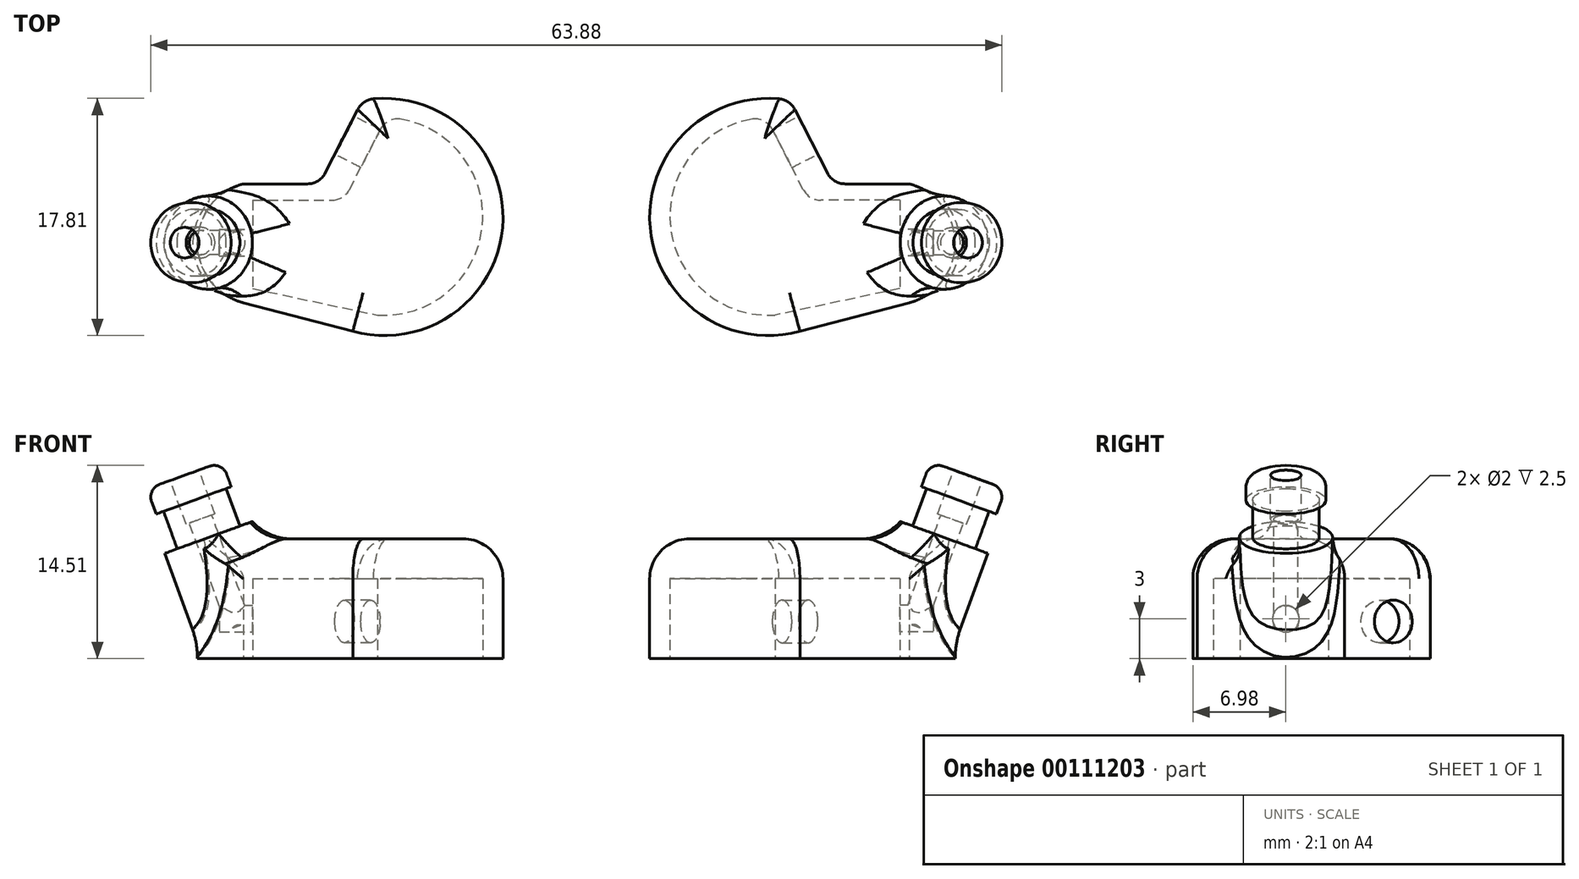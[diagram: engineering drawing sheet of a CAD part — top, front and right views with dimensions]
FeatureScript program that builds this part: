
annotation { "Feature Type Name" : "Feature", "Feature Type Description" : "" }
export const myFeature = defineFeature(function(context is Context, id is Id, definition is map)
    precondition{}
    {
        {
            var Q0;
            Q0=qCreatedBy(makeId("Top.planeOp"),FACE);
            var sketch = newSketch(context, id + "F0", { "sketchPlane" : qUnion([Q0])});
            skLineSegment(sketch, "E0", {"start": v(0, 4.41) * mm, "end": v(5.73, 4.41) * mm});
            skLineSegment(sketch, "E1", {"start": v(5.73, 4.41) * mm, "end": v(8.95, 10.68) * mm});
            skLineSegment(sketch, "E2", {"start": v(0, -4.5) * mm, "end": v(8.22, -6.66) * mm});
            skArc(sketch, "E3", {"start": v(8.22, -6.66) * mm, "mid": v(19.49, 1.55) * mm, "end": v(8.95, 10.68) * mm});
            skArc(sketch, "E4", {"start": v(0, 4.41) * mm, "mid": v(-3.44, -0.05) * mm, "end": v(0, -4.5) * mm});
            skSolve(sketch);
        }
        {
            var Q0;
            Q0=makeQuery(id+"F0.imprint","IMPRINT",FACE,{"disambiguationData":[TD([[makeQuery(id+"F0.imprint","IMPRINT",EDGE,{"derivedFrom":sQuery(id+"F0.wireOp",EDGE,"E0")}),-1.0]])]});
            extrude(context, id + "F1", {"entities" : qUnion([Q0]), "depth" : 9 * mm});
        }
        {
            var Q0;
            Q0=makeQuery(id+"F1.opExtrude","CAP_FACE",FACE,{"disambiguationData":[OSD([sQuery(id+"F0.wireOp",EDGE,"E0"),sQuery(id+"F0.wireOp",EDGE,"E1"),sQuery(id+"F0.wireOp",EDGE,"E2"),sQuery(id+"F0.wireOp",EDGE,"E3"),sQuery(id+"F0.wireOp",EDGE,"E4")])],"isStart":true});
            var sketch = newSketch(context, id + "F2", { "sketchPlane" : qUnion([Q0])});
            skLineSegment(sketch, "E5", {"start": v(0.7, -3.18) * mm, "end": v(0.7, 3.44) * mm});
            skLineSegment(sketch, "E6", {"start": v(0.7, 3.44) * mm, "end": v(10.06, 5.44) * mm});
            skLineSegment(sketch, "E7", {"start": v(0.7, -3.18) * mm, "end": v(7.56, -3.18) * mm});
            skLineSegment(sketch, "E8", {"start": v(7.56, -3.18) * mm, "end": v(10.74, -9.38) * mm});
            skArc(sketch, "E9", {"start": v(10.74, -9.38) * mm, "mid": v(17.97, -1.63) * mm, "end": v(10.06, 5.44) * mm});
            skSolve(sketch);
        }
        {
            var Q0;
            Q0=makeQuery(id+"F2.imprint","IMPRINT",FACE,{"disambiguationData":[TD([[makeQuery(id+"F2.imprint","IMPRINT",EDGE,{"derivedFrom":sQuery(id+"F2.wireOp",EDGE,"E5")}),-1.0]])]});
            extrude(context, id + "F3", {"entities" : qUnion([Q0]), "operationType" : NewBodyOperationType.REMOVE, "oppositeDirection" : true, "depth" : 6 * mm});
        }
        {
            var Q0;
            Q0=makeQuery(id+"F3.boolean.opBoolean","COPY",FACE,{"derivedFrom":makeQuery(id+"F3.opExtrude","SWEPT_FACE",FACE,{"disambiguationData":[OSD([sQuery(id+"F2.wireOp",EDGE,"E5")])]})});
            var sketch = newSketch(context, id + "F4", { "sketchPlane" : qUnion([Q0])});
            skCircle(sketch, "E10", {"center": v(0, 3) * mm, "radius": 1 * mm});
            skPoint(sketch, "E10.centerSnap0", {"position": v(3.18, 3) * mm});
            skSolve(sketch);
        }
        {
            var Q0;
            Q0=qCreatedBy(makeId("Top.planeOp"),FACE);
            var sketch = newSketch(context, id + "F5", { "sketchPlane" : qUnion([Q0])});
            skLineSegment(sketch, "E11", {"start": v(-2.42, 7.93) * mm, "end": v(-2.42, -5.03) * mm});
            skSolve(sketch);
        }
        {
            var Q0;
            Q0=makeQuery(id+"F1.opExtrude","CAP_FACE",FACE,{"disambiguationData":[OSD([sQuery(id+"F0.wireOp",EDGE,"E0"),sQuery(id+"F0.wireOp",EDGE,"E1"),sQuery(id+"F0.wireOp",EDGE,"E2"),sQuery(id+"F0.wireOp",EDGE,"E3"),sQuery(id+"F0.wireOp",EDGE,"E4")])],"isStart":true});
            var Q1;
            Q1=sQuery(id+"F5.wireOp",EDGE,"E11");
            cPlane(context, id + "F6", {"entities" : qUnion([Q0, Q1]), "cplaneType" : CPlaneType.LINE_ANGLE, "offset" : 25 * mm, "angle" : 0 * degree, "width" : 150 * mm, "height" : 150 * mm});
        }
        {
            var Q0;
            Q0=qCreatedBy(id+"F6.planeOp",FACE);
            var sketch = newSketch(context, id + "F7", { "sketchPlane" : qUnion([Q0])});
            skCircle(sketch, "E12", {"center": v(-2.08, 0) * mm, "radius": 1 * mm});
            skSolve(sketch);
        }
        {
            var Q0;
            Q0=qSketchRegion(id+"F7",true);
            extrude(context, id + "F8", {"entities" : qUnion([Q0]), "operationType" : NewBodyOperationType.REMOVE, "endBound" : BoundingType.THROUGH_ALL, "oppositeDirection" : true, "depth" : 25 * mm});
        }
        {
            var Q0;
            {var subQ0=sQuery(id+"F0.wireOp",EDGE,"E4");var subQ1=sQuery(id+"F0.wireOp",EDGE,"E1");var subQ2=sQuery(id+"F0.wireOp",EDGE,"E0");var subQ3=sQuery(id+"F0.wireOp",EDGE,"E2");var subQ4=sQuery(id+"F0.wireOp",EDGE,"E3");Q0=makeQuery(id+"FRAegpGUTcR0WfW_1.boolean.opBoolean","SPLIT",FACE,{"disambiguationData":[TD([makeQuery(id+"F1.opExtrude","SWEPT_FACE",FACE,{"disambiguationData":[OSD([subQ2])]}),makeQuery(id+"F1.opExtrude","SWEPT_FACE",FACE,{"disambiguationData":[OSD([subQ1])]}),makeQuery(id+"F1.opExtrude","SWEPT_FACE",FACE,{"disambiguationData":[OSD([subQ3])]}),makeQuery(id+"F1.opExtrude","SWEPT_FACE",FACE,{"disambiguationData":[OSD([subQ4])]}),makeQuery(id+"F1.opExtrude","SWEPT_FACE",FACE,{"disambiguationData":[OSD([subQ0])]}),makeQuery(id+"F3.boolean.opBoolean","COPY",FACE,{"derivedFrom":makeQuery(id+"F3.opExtrude","SWEPT_FACE",FACE,{"disambiguationData":[OSD([sQuery(id+"F2.wireOp",EDGE,"E5")])]})}),makeQuery(id+"F3.boolean.opBoolean","COPY",FACE,{"derivedFrom":makeQuery(id+"F3.opExtrude","SWEPT_FACE",FACE,{"disambiguationData":[OSD([sQuery(id+"F2.wireOp",EDGE,"E6")])]})}),makeQuery(id+"F3.boolean.opBoolean","COPY",FACE,{"derivedFrom":makeQuery(id+"F3.opExtrude","SWEPT_FACE",FACE,{"disambiguationData":[OSD([sQuery(id+"F2.wireOp",EDGE,"E7")])]})}),makeQuery(id+"F3.boolean.opBoolean","COPY",FACE,{"derivedFrom":makeQuery(id+"F3.opExtrude","SWEPT_FACE",FACE,{"disambiguationData":[OSD([sQuery(id+"F2.wireOp",EDGE,"E8")])]})}),makeQuery(id+"F3.boolean.opBoolean","COPY",FACE,{"derivedFrom":makeQuery(id+"F3.opExtrude","SWEPT_FACE",FACE,{"disambiguationData":[OSD([sQuery(id+"F2.wireOp",EDGE,"E9")])]})}),makeQuery(id+"FRAegpGUTcR0WfW_1.opExtrude","SWEPT_FACE",FACE,{"disambiguationData":[OSD([sQuery(id+"F8U8vHJtzTjUuwL_1.wireOp",EDGE,"gdrP36Y7-fI1G-Q2D7-S0Vl-d63eQvXMdG0R")])]})])],"derivedFrom":makeQuery(id+"F1.opExtrude","CAP_FACE",FACE,{"disambiguationData":[OSD([subQ2,subQ1,subQ3,subQ4,subQ0])],"isStart":true})});}
            var sketch = newSketch(context, id + "F9", { "sketchPlane" : qUnion([Q0])});
            skLineSegment(sketch, "E13.bottom", {"start": v(0.7, -3.18) * mm, "end": v(3.3, -3.18) * mm});
            skLineSegment(sketch, "E13.top", {"start": v(0.7, 2.54) * mm, "end": v(3.3, 2.54) * mm});
            skLineSegment(sketch, "E13.left", {"start": v(0.7, -3.18) * mm, "end": v(0.7, 2.54) * mm});
            skLineSegment(sketch, "E13.right", {"start": v(3.3, -3.18) * mm, "end": v(3.3, 2.54) * mm});
            skSolve(sketch);
        }
        {
            var Q0;
            Q0=qCreatedBy(id+"F6.planeOp",FACE);
            cPlane(context, id + "F10", {"entities" : qUnion([Q0]), "cplaneType" : CPlaneType.OFFSET, "offset" : 8 * mm, "width" : 150 * mm, "height" : 150 * mm});
        }
        {
            var Q0;
            Q0=qCreatedBy(id+"F10.planeOp",FACE);
            var sketch = newSketch(context, id + "F11", { "sketchPlane" : qUnion([Q0])});
            skLineSegment(sketch, "E14", {"start": v(-2.42, 7.93) * mm, "end": v(-2.42, -5.03) * mm});
            skSolve(sketch);
        }
        {
            var Q0;
            Q0=makeQuery(id+"F1.opExtrude","CAP_FACE",FACE,{"disambiguationData":[OSD([sQuery(id+"F0.wireOp",EDGE,"E0"),sQuery(id+"F0.wireOp",EDGE,"E1"),sQuery(id+"F0.wireOp",EDGE,"E2"),sQuery(id+"F0.wireOp",EDGE,"E3"),sQuery(id+"F0.wireOp",EDGE,"E4")])],"isStart":false});
            var Q1;
            Q1=sQuery(id+"F11.wireOp",EDGE,"E14");
            cPlane(context, id + "F12", {"entities" : qUnion([Q0, Q1]), "cplaneType" : CPlaneType.LINE_ANGLE, "offset" : 25 * mm, "angle" : 20 * degree, "width" : 150 * mm, "height" : 150 * mm});
        }
        {
            var Q0;
            Q0=qCreatedBy(id+"F12.planeOp",FACE);
            var sketch = newSketch(context, id + "F13", { "sketchPlane" : qUnion([Q0])});
            skCircle(sketch, "E15", {"center": v(0.67, 0) * mm, "radius": 3.5 * mm});
            skSolve(sketch);
        }
        {
            var Q0;
            Q0=qSketchRegion(id+"F13",true);
            extrude(context, id + "F14", {"entities" : qUnion([Q0]), "operationType" : NewBodyOperationType.ADD, "depth" : 6.5 * mm});
        }
        {
            var Q0;
            Q0=qSketchRegion(id+"F13",true);
            extrude(context, id + "F15", {"entities" : qUnion([Q0]), "operationType" : NewBodyOperationType.ADD, "oppositeDirection" : true, "depth" : 1.1 * mm});
        }
        {
            var Q0;
            Q0=makeQuery(id+"F15.opExtrude","CAP_FACE",FACE,{"disambiguationData":[OSD([sQuery(id+"F13.wireOp",EDGE,"E15")])],"isStart":false});
            var sketch = newSketch(context, id + "F16", { "sketchPlane" : qUnion([Q0])});
            skCircle(sketch, "E16", {"center": v(0.67, 0) * mm, "radius": 2.5 * mm});
            skSolve(sketch);
        }
        {
            var Q0;
            Q0=qSketchRegion(id+"F16",true);
            extrude(context, id + "F17", {"entities" : qUnion([Q0]), "operationType" : NewBodyOperationType.ADD, "depth" : 3 * mm});
        }
        {
            var Q0;
            Q0=makeQuery(id+"F17.opExtrude","CAP_FACE",FACE,{"disambiguationData":[OSD([sQuery(id+"F16.wireOp",EDGE,"E16")])],"isStart":false});
            var sketch = newSketch(context, id + "F18", { "sketchPlane" : qUnion([Q0])});
            skCircle(sketch, "E17", {"center": v(0.57, 0) * mm, "radius": 3 * mm});
            skSolve(sketch);
        }
        {
            var Q0;
            Q0=qSketchRegion(id+"F18",true);
            extrude(context, id + "F19", {"entities" : qUnion([Q0]), "operationType" : NewBodyOperationType.ADD, "depth" : 2 * mm});
        }
        {
            var Q0;
            Q0=makeQuery(id+"F19.opExtrude","CAP_FACE",FACE,{"disambiguationData":[OSD([sQuery(id+"F18.wireOp",EDGE,"E17")])],"isStart":false});
            var sketch = newSketch(context, id + "F20", { "sketchPlane" : qUnion([Q0])});
            skCircle(sketch, "E18", {"center": v(0.57, 0) * mm, "radius": 0.9 * mm});
            skSolve(sketch);
        }
        {
            var Q0;
            Q0=qSketchRegion(id+"F20",true);
            extrude(context, id + "F21", {"entities" : qUnion([Q0]), "operationType" : NewBodyOperationType.REMOVE, "oppositeDirection" : true, "depth" : 12 * mm});
        }
        {
            var Q0;
            Q0=makeQuery(id+"F4.imprint","IMPRINT",FACE,{"disambiguationData":[TD([[makeQuery(id+"F4.imprint","IMPRINT",EDGE,{"derivedFrom":sQuery(id+"F4.wireOp",EDGE,"E10")}),1.0]])]});
            extrude(context, id + "F22", {"entities" : qUnion([Q0]), "operationType" : NewBodyOperationType.REMOVE, "oppositeDirection" : true, "depth" : 2.5 * mm});
        }
        {
            var Q0;
            Q0=qSketchRegion(id+"F9",true);
            extrude(context, id + "F23", {"entities" : qUnion([Q0]), "operationType" : NewBodyOperationType.REMOVE, "oppositeDirection" : true, "depth" : 5 * mm});
        }
        {
            var Q0;
            Q0=makeQuery(id+"F19.opExtrude","CAP_EDGE",EDGE,{"disambiguationData":[OSD([sQuery(id+"F18.wireOp",EDGE,"E17")])],"isStart":false});
            fillet(context, id + "F24", {"entities" : qUnion([Q0]), "radius" : 1 * mm, "tangentPropagation" : true, "allowEdgeOverflow" : false});
        }
        {
            var Q0;
            Q0=makeQuery(id+"F1.opExtrude","SWEPT_EDGE",EDGE,{"disambiguationData":[OSD([sQuery(id+"F0.wireOp",EDGE,"E1"),sQuery(id+"F0.wireOp",EDGE,"E3")])]});
            var Q1;
            Q1=makeQuery(id+"F1.opExtrude","SWEPT_EDGE",EDGE,{"disambiguationData":[OSD([sQuery(id+"F0.wireOp",EDGE,"E0"),sQuery(id+"F0.wireOp",EDGE,"E1")])]});
            var Q2;
            Q2=makeQuery(id+"F3.boolean.opBoolean","COPY",EDGE,{"derivedFrom":makeQuery(id+"F3.opExtrude","SWEPT_EDGE",EDGE,{"disambiguationData":[OSD([sQuery(id+"F2.wireOp",EDGE,"E7"),sQuery(id+"F2.wireOp",EDGE,"E8")])]})});
            var Q3;
            Q3=makeQuery(id+"F3.boolean.opBoolean","COPY",EDGE,{"derivedFrom":makeQuery(id+"F3.opExtrude","SWEPT_EDGE",EDGE,{"disambiguationData":[OSD([sQuery(id+"F2.wireOp",EDGE,"E8"),sQuery(id+"F2.wireOp",EDGE,"E9")])]})});
            fillet(context, id + "F25", {"entities" : qUnion([Q0, Q1, Q2, Q3]), "radius" : 1.5 * mm, "tangentPropagation" : true, "allowEdgeOverflow" : false});
        }
        {
            var Q0;
            Q0=makeQuery(id+"F1.opExtrude","CAP_FACE",FACE,{"disambiguationData":[OSD([sQuery(id+"F0.wireOp",EDGE,"E0"),sQuery(id+"F0.wireOp",EDGE,"E1"),sQuery(id+"F0.wireOp",EDGE,"E2"),sQuery(id+"F0.wireOp",EDGE,"E3"),sQuery(id+"F0.wireOp",EDGE,"E4")])],"isStart":true});
            var sketch = newSketch(context, id + "F26", { "sketchPlane" : qUnion([Q0])});
            skLineSegment(sketch, "E19.bottom", {"start": v(0.7, -3.18) * mm, "end": v(3.41, -3.18) * mm});
            skLineSegment(sketch, "E19.top", {"start": v(0.7, 3.44) * mm, "end": v(3.41, 3.44) * mm});
            skLineSegment(sketch, "E19.left", {"start": v(0.7, -3.18) * mm, "end": v(0.7, 3.44) * mm});
            skLineSegment(sketch, "E19.right", {"start": v(3.41, -3.18) * mm, "end": v(3.41, 3.44) * mm});
            skSolve(sketch);
        }
        {
            var Q0;
            Q0=qSketchRegion(id+"F26",true);
            extrude(context, id + "F27", {"entities" : qUnion([Q0]), "operationType" : NewBodyOperationType.REMOVE, "oppositeDirection" : true, "depth" : 5.5 * mm});
        }
        {
            var Q0;
            Q0=makeQuery(id+"F1.opExtrude","SWEPT_FACE",FACE,{"disambiguationData":[OSD([sQuery(id+"F0.wireOp",EDGE,"E1")])]});
            var sketch = newSketch(context, id + "F28", { "sketchPlane" : qUnion([Q0])});
            skCircle(sketch, "E20", {"center": v(-10.64, 2.8) * mm, "radius": 1.6 * mm});
            skSolve(sketch);
        }
        {
            var Q0;
            Q0=makeQuery(id+"F28.imprint","IMPRINT",FACE,{"disambiguationData":[TD([[makeQuery(id+"F28.imprint","IMPRINT",EDGE,{"derivedFrom":sQuery(id+"F28.wireOp",EDGE,"E20")}),1.0]])]});
            extrude(context, id + "F29", {"entities" : qUnion([Q0]), "operationType" : NewBodyOperationType.REMOVE, "endBound" : BoundingType.UP_TO_NEXT, "oppositeDirection" : true, "depth" : 25 * mm});
        }
        {
            var Q0;
            Q0=qSketchRegion(id+"F26",true);
            extrude(context, id + "F30", {"entities" : qUnion([Q0]), "operationType" : NewBodyOperationType.REMOVE, "oppositeDirection" : true, "depth" : 6 * mm});
        }
        {
            var Q0;
            Q0=makeQuery(id+"F1.opExtrude","CAP_EDGE",EDGE,{"disambiguationData":[OSD([sQuery(id+"F0.wireOp",EDGE,"E0")])],"isStart":false});
            fillet(context, id + "F31", {"entities" : qUnion([Q0]), "radius" : 3 * mm, "tangentPropagation" : true, "allowEdgeOverflow" : false});
        }
        {
            var Q0;
            {var subQ0=sQuery(id+"F13.wireOp",EDGE,"E15");var subQ1=sQuery(id+"F0.wireOp",EDGE,"E4");var subQ2=sQuery(id+"F0.wireOp",EDGE,"E2");Q0=makeQuery(id+"F31.opFillet","BLEND_EDGE",EDGE,{"blendedFrom":[makeQuery(id+"F1.opExtrude","CAP_EDGE",EDGE,{"disambiguationData":[OSD([subQ2])],"isStart":false}),makeQuery(id+"F15.boolean.opBoolean","MERGE",FACE,{"derivedFrom":[makeQuery(id+"F14.boolean.opBoolean","SPLIT",FACE,{"disambiguationData":[TD([makeQuery(id+"F1.opExtrude","SWEPT_FACE",FACE,{"disambiguationData":[OSD([subQ1])]})])],"derivedFrom":makeQuery(id+"F14.opExtrude","SWEPT_FACE",FACE,{"disambiguationData":[OSD([subQ0])]})}),makeQuery(id+"F15.opExtrude","SWEPT_FACE",FACE,{"disambiguationData":[OSD([subQ0])]})]})],"blendedInto":[makeQuery(id+"F15.boolean.opBoolean","MERGE",FACE,{"derivedFrom":[makeQuery(id+"F14.boolean.opBoolean","SPLIT",FACE,{"disambiguationData":[TD([makeQuery(id+"F1.opExtrude","SWEPT_FACE",FACE,{"disambiguationData":[OSD([subQ1])]})])],"derivedFrom":makeQuery(id+"F14.opExtrude","SWEPT_FACE",FACE,{"disambiguationData":[OSD([subQ0])]})}),makeQuery(id+"F15.opExtrude","SWEPT_FACE",FACE,{"disambiguationData":[OSD([subQ0])]})]})]});}
            fillet(context, id + "F32", {"entities" : qUnion([Q0]), "radius" : 4 * mm, "tangentPropagation" : true, "allowEdgeOverflow" : false});
        }
        {
            var Q0;
            Q0=makeQuery(id+"F19.opExtrude","CAP_FACE",FACE,{"disambiguationData":[OSD([sQuery(id+"F18.wireOp",EDGE,"E17")])],"isStart":false});
            var sketch = newSketch(context, id + "F33", { "sketchPlane" : qUnion([Q0])});
            skCircle(sketch, "E21", {"center": v(0.57, 0) * mm, "radius": 1.15 * mm});
            skSolve(sketch);
        }
        {
            var Q0;
            Q0=makeQuery(id+"F33.imprint","IMPRINT",FACE,{"disambiguationData":[TD([[makeQuery(id+"F33.imprint","IMPRINT",EDGE,{"derivedFrom":sQuery(id+"F33.wireOp",EDGE,"E21")}),1.0]])]});
            var Q1;
            Q1=sQuery(id+"F33.wireOp",EDGE,"E21");
            extrude(context, id + "F34", {"entities" : qUnion([Q0]), "operationType" : NewBodyOperationType.REMOVE, "surfaceEntities" : qUnion([Q1]), "oppositeDirection" : true, "depth" : 3.5 * mm});
        }
        {
            var Q0;
            Q0=makeQuery(id+"F15.boolean.opBoolean","INTERSECT",EDGE,{"disambiguationData":[OD(0.0)],"derivedFrom":[makeQuery(id+"F1.opExtrude","SWEPT_FACE",FACE,{"disambiguationData":[OSD([sQuery(id+"F0.wireOp",EDGE,"E4")])]}),makeQuery(id+"F15.opExtrude","SWEPT_FACE",FACE,{"disambiguationData":[OSD([sQuery(id+"F13.wireOp",EDGE,"E15")])]})]});
            var Q1;
            Q1=makeQuery(id+"F15.boolean.opBoolean","INTERSECT",EDGE,{"disambiguationData":[OD(1.0)],"derivedFrom":[makeQuery(id+"F1.opExtrude","SWEPT_FACE",FACE,{"disambiguationData":[OSD([sQuery(id+"F0.wireOp",EDGE,"E4")])]}),makeQuery(id+"F15.opExtrude","SWEPT_FACE",FACE,{"disambiguationData":[OSD([sQuery(id+"F13.wireOp",EDGE,"E15")])]})]});
            fillet(context, id + "F35", {"entities" : qUnion([Q0, Q1]), "radius" : 6 * mm, "tangentPropagation" : true, "allowEdgeOverflow" : false});
        }
        {
            var Q0;
            Q0=qCreatedBy(makeId("Right.planeOp"),FACE);
            cPlane(context, id + "F36", {"entities" : qUnion([Q0]), "cplaneType" : CPlaneType.OFFSET, "offset" : 25 * mm, "width" : 150 * mm, "height" : 150 * mm});
        }
        {
            var Q0;
            Q0=makeQuery(id+"F1.opExtrude","SWEPT_BODY",BODY,{"disambiguationData":[OSD([sQuery(id+"F0.wireOp",EDGE,"E0"),sQuery(id+"F0.wireOp",EDGE,"E1"),sQuery(id+"F0.wireOp",EDGE,"E2"),sQuery(id+"F0.wireOp",EDGE,"E3"),sQuery(id+"F0.wireOp",EDGE,"E4")])]});
            var Q1;
            Q1=qCreatedBy(id+"F36.planeOp",FACE);
            mirror(context, id + "F37", {"entities" : qUnion([Q0]), "mirrorPlane" : qUnion([Q1])});
        }
    });
